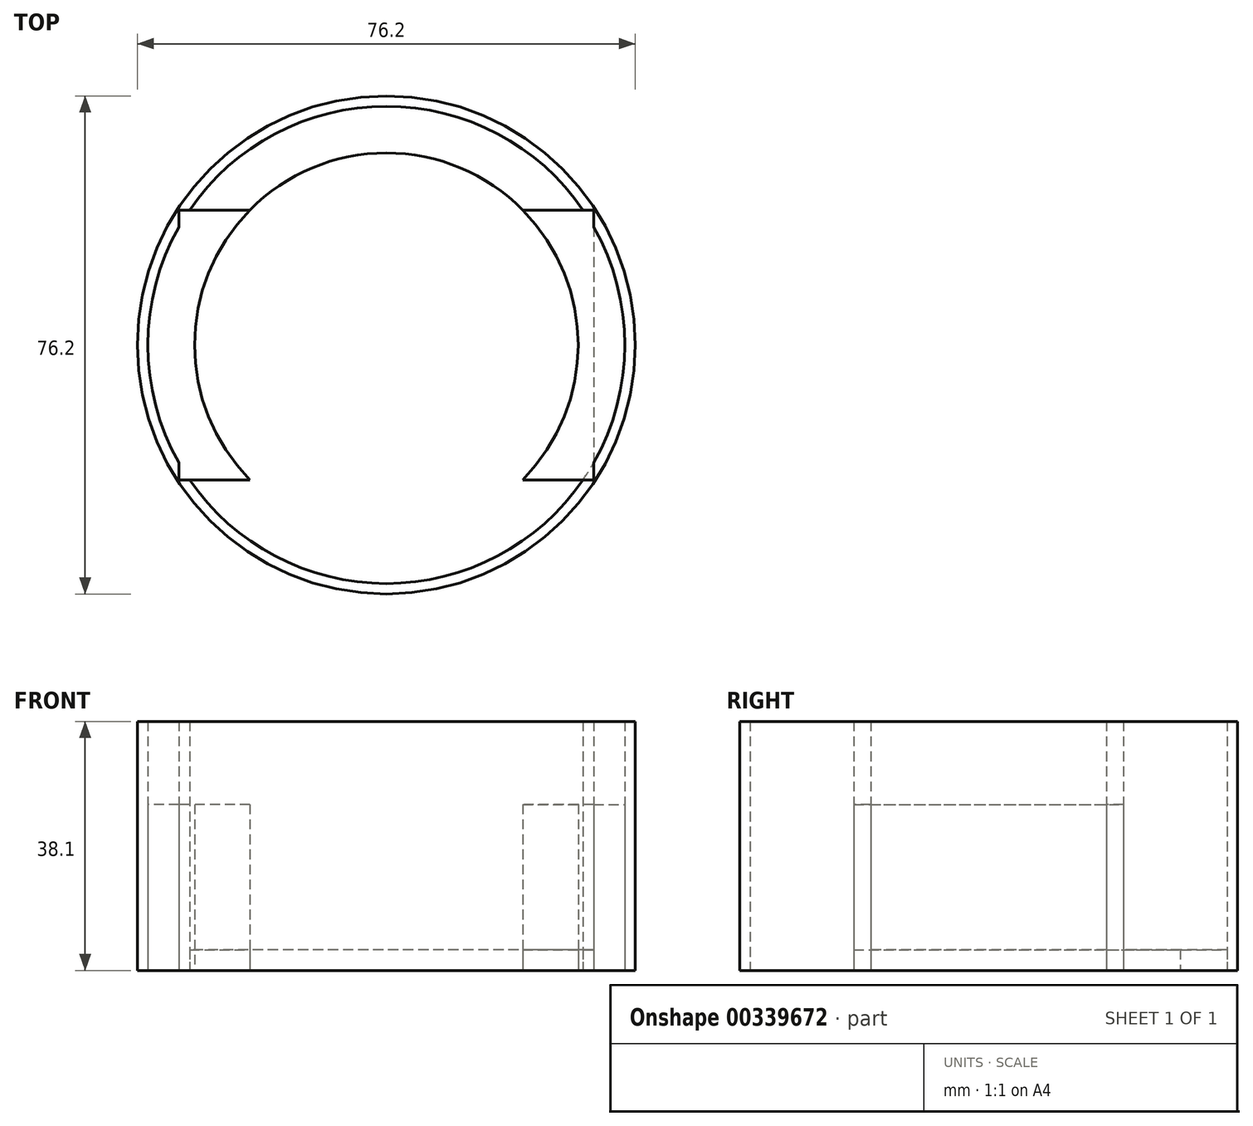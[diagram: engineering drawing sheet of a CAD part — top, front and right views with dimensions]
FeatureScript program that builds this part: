
annotation { "Feature Type Name" : "Feature", "Feature Type Description" : "" }
export const myFeature = defineFeature(function(context is Context, id is Id, definition is map)
    precondition{}
    {
        {
            var Q0;
            Q0=qCreatedBy(makeId("Top.planeOp"),FACE);
            var sketch = newSketch(context, id + "F0", { "sketchPlane" : qUnion([Q0])});
            skCircle(sketch, "E0", {"center": v(0, 0) * mm, "radius": 38.1 * mm});
            skCircle(sketch, "E1", {"center": v(0, 0) * mm, "radius": 29.37 * mm});
            skCircle(sketch, "E2", {"center": v(0, 0) * mm, "radius": 36.51 * mm});
            skLineSegment(sketch, "E3", {"start": v(31.75, 21.06) * mm, "end": v(31.75, -21.06) * mm});
            skLineSegment(sketch, "E4", {"start": v(-31.75, -21.06) * mm, "end": v(-31.75, 0) * mm});
            skLineSegment(sketch, "E5", {"start": v(-31.75, 0) * mm, "end": v(-31.75, 20.64) * mm});
            skLineSegment(sketch, "E6", {"start": v(-31.75, 20.64) * mm, "end": v(32.03, 20.64) * mm});
            skLineSegment(sketch, "E7", {"start": v(32.03, -20.64) * mm, "end": v(-32.03, -20.64) * mm});
            skPoint(sketch, "E8.start.orphan", {"position": v(0, 46.48) * mm});
            skSolve(sketch);
        }
        {
            var Q0;
            {var subQ0=sQuery(id+"F0.wireOp",EDGE,"E6");var subQ1=sQuery(id+"F0.wireOp",EDGE,"E1");var subQ2=makeQuery(id+"F0.imprint","INTERSECT",VERTEX,{"disambiguationData":[OD(0.0)],"derivedFrom":[subQ1,subQ0]});Q0=makeQuery(id+"F0.imprint","IMPRINT",FACE,{"disambiguationData":[TD([[makeQuery(id+"F0.imprint","IMPRINT",EDGE,{"disambiguationData":[TD([[subQ2,1.0]])],"derivedFrom":subQ1}),-1.0]])]});}
            var Q1;
            {var subQ0=sQuery(id+"F0.wireOp",EDGE,"E7");var subQ1=sQuery(id+"F0.wireOp",EDGE,"E1");var subQ2=makeQuery(id+"F0.imprint","INTERSECT",VERTEX,{"disambiguationData":[OD(0.0)],"derivedFrom":[subQ1,subQ0]});Q1=makeQuery(id+"F0.imprint","IMPRINT",FACE,{"disambiguationData":[TD([[makeQuery(id+"F0.imprint","IMPRINT",EDGE,{"disambiguationData":[TD([[subQ2,-1.0]])],"derivedFrom":subQ1}),-1.0]])]});}
            extrude(context, id + "F1", {"entities" : qUnion([Q0, Q1]), "depth" : 3.17 * mm});
        }
        {
            var Q0;
            Q0 = qSketchRegion(id + "F0", true);
            extrude(context, id + "F2", {"entities" : qUnion([Q0]), "depth" : 38.1 * mm});
        }
        {
            var Q0;
            {var subQ6=sQuery(id+"F0.wireOp",EDGE,"E6");var subQ7=sQuery(id+"F0.wireOp",EDGE,"E1");var subQ8=makeQuery(id+"F0.imprint","INTERSECT",VERTEX,{"disambiguationData":[OD(1.0)],"derivedFrom":[subQ7,subQ6]});Q0=makeQuery(id+"F0.imprint","IMPRINT",FACE,{"disambiguationData":[TD([[makeQuery(id+"F0.imprint","IMPRINT",EDGE,{"disambiguationData":[TD([[subQ8,1.0]])],"derivedFrom":subQ7}),-1.0]])]});}
            var Q1;
            {var subQ7=sQuery(id+"F0.wireOp",EDGE,"E6");var subQ10=sQuery(id+"F0.wireOp",EDGE,"E1");var subQ11=makeQuery(id+"F0.imprint","INTERSECT",VERTEX,{"disambiguationData":[OD(0.0)],"derivedFrom":[subQ10,subQ7]});Q1=makeQuery(id+"F0.imprint","IMPRINT",FACE,{"disambiguationData":[TD([[makeQuery(id+"F0.imprint","IMPRINT",EDGE,{"disambiguationData":[TD([[subQ11,-1.0]])],"derivedFrom":subQ10}),-1.0]])]});}
            var Q2;
            {var subQ0=sQuery(id+"F0.wireOp",EDGE,"E5");var subQ1=sQuery(id+"F0.wireOp",EDGE,"E2");var subQ2=makeQuery(id+"F0.imprint","INTERSECT",VERTEX,{"derivedFrom":[subQ1,subQ0]});Q2=makeQuery(id+"F0.imprint","IMPRINT",FACE,{"disambiguationData":[TD([[makeQuery(id+"F0.imprint","IMPRINT",EDGE,{"disambiguationData":[TD([[subQ2,-1.0]])],"derivedFrom":subQ1}),1.0]])]});}
            var Q3;
            {var subQ0=sQuery(id+"F0.wireOp",EDGE,"E3");var subQ1=sQuery(id+"F0.wireOp",EDGE,"E2");var subQ2=makeQuery(id+"F0.imprint","INTERSECT",VERTEX,{"disambiguationData":[OD(0.0)],"derivedFrom":[subQ1,subQ0]});Q3=makeQuery(id+"F0.imprint","IMPRINT",FACE,{"disambiguationData":[TD([[makeQuery(id+"F0.imprint","IMPRINT",EDGE,{"disambiguationData":[TD([[subQ2,1.0]])],"derivedFrom":subQ1}),1.0]])]});}
            var Q4;
            {var subQ0=sQuery(id+"F0.wireOp",EDGE,"E6");var subQ1=sQuery(id+"F0.wireOp",EDGE,"E2");var subQ2=makeQuery(id+"F0.imprint","INTERSECT",VERTEX,{"disambiguationData":[OD(1.0)],"derivedFrom":[subQ1,subQ0]});Q4=makeQuery(id+"F0.imprint","IMPRINT",FACE,{"disambiguationData":[TD([[makeQuery(id+"F0.imprint","IMPRINT",EDGE,{"disambiguationData":[TD([[subQ2,-1.0]])],"derivedFrom":subQ1}),-1.0]])]});}
            var Q5;
            {var subQ0=sQuery(id+"F0.wireOp",EDGE,"E4");var subQ1=sQuery(id+"F0.wireOp",EDGE,"E2");var subQ2=makeQuery(id+"F0.imprint","INTERSECT",VERTEX,{"derivedFrom":[subQ1,subQ0]});Q5=makeQuery(id+"F0.imprint","IMPRINT",FACE,{"disambiguationData":[TD([[makeQuery(id+"F0.imprint","IMPRINT",EDGE,{"disambiguationData":[TD([[subQ2,-1.0]])],"derivedFrom":subQ1}),-1.0]])]});}
            var Q6;
            {var subQ0=sQuery(id+"F0.wireOp",EDGE,"E7");var subQ1=sQuery(id+"F0.wireOp",EDGE,"E2");var subQ2=makeQuery(id+"F0.imprint","INTERSECT",VERTEX,{"disambiguationData":[OD(1.0)],"derivedFrom":[subQ1,subQ0]});Q6=makeQuery(id+"F0.imprint","IMPRINT",FACE,{"disambiguationData":[TD([[makeQuery(id+"F0.imprint","IMPRINT",EDGE,{"disambiguationData":[TD([[subQ2,-1.0]])],"derivedFrom":subQ1}),-1.0]])]});}
            var Q7;
            {var subQ0=sQuery(id+"F0.wireOp",EDGE,"E6");var subQ1=sQuery(id+"F0.wireOp",EDGE,"E2");var subQ2=makeQuery(id+"F0.imprint","INTERSECT",VERTEX,{"disambiguationData":[OD(0.0)],"derivedFrom":[subQ1,subQ0]});Q7=makeQuery(id+"F0.imprint","IMPRINT",FACE,{"disambiguationData":[TD([[makeQuery(id+"F0.imprint","IMPRINT",EDGE,{"disambiguationData":[TD([[subQ2,1.0]])],"derivedFrom":subQ1}),-1.0]])]});}
            extrude(context, id + "F3", {"entities" : qUnion([Q0, Q1, Q2, Q3, Q4, Q5, Q6, Q7]), "depth" : 25.4 * mm});
        }
    });
